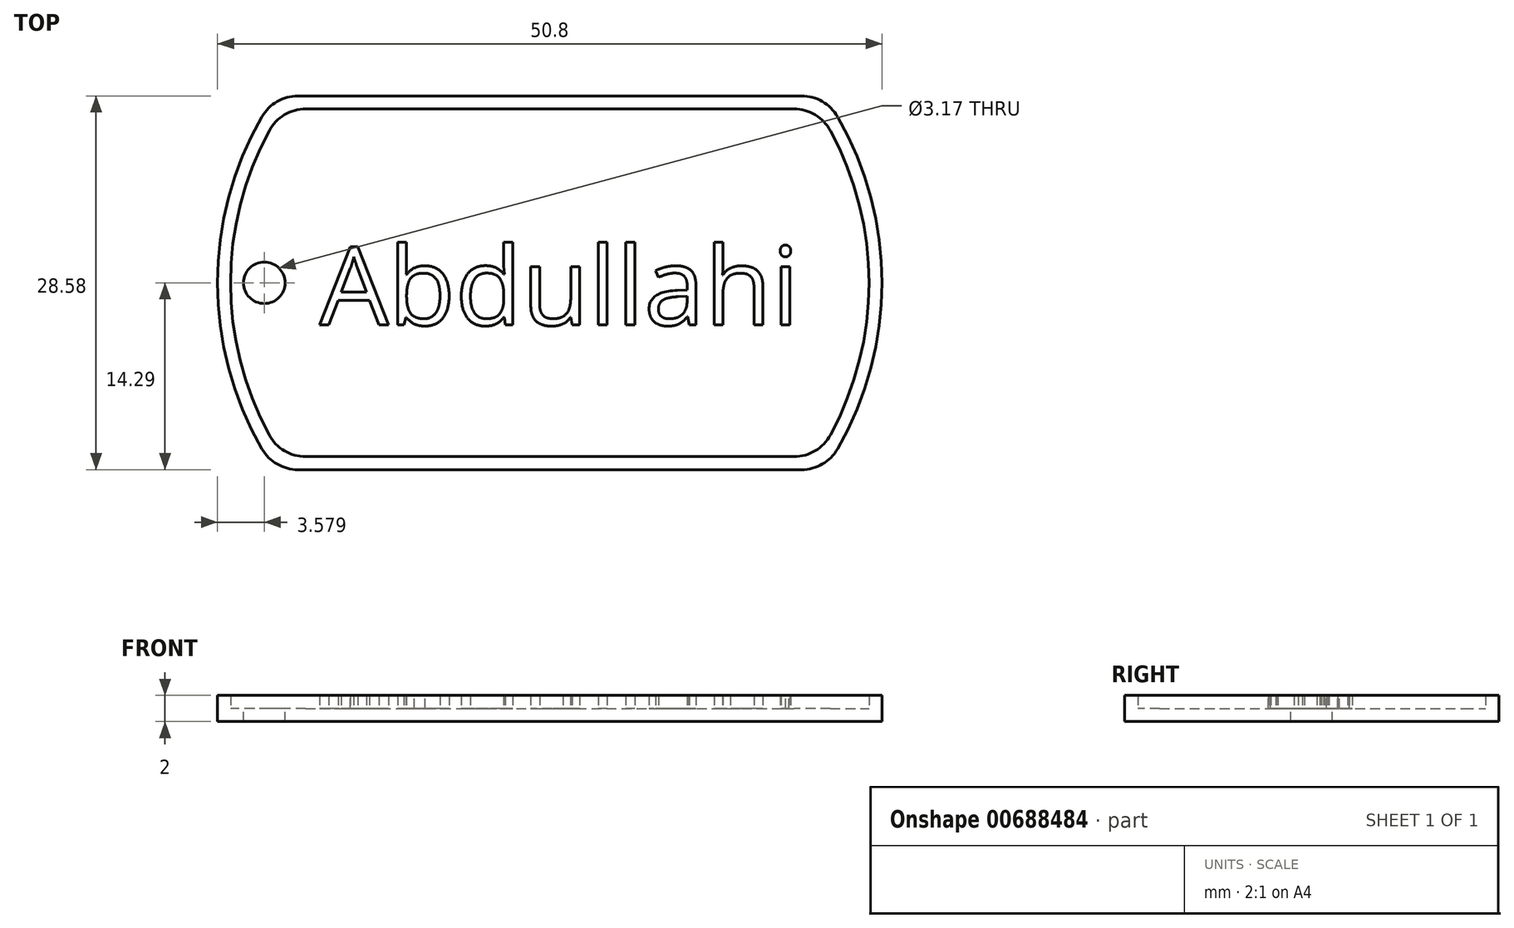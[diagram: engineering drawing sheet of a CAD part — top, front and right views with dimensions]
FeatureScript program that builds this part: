
annotation { "Feature Type Name" : "Feature", "Feature Type Description" : "" }
export const myFeature = defineFeature(function(context is Context, id is Id, definition is map)
    precondition{}
    {
        {
            var Q0;
            Q0=qCreatedBy(makeId("Top.planeOp"),FACE);
            var sketch = newSketch(context, id + "F0", { "sketchPlane" : qUnion([Q0])});
            skArc(sketch, "E0", {"start": v(-22, 12.7) * mm, "mid": v(-25.4, 0) * mm, "end": v(-22, -12.7) * mm});
            skLineSegment(sketch, "E1.top", {"start": v(-19.25, -14.29) * mm, "end": v(19.25, -14.29) * mm});
            skArc(sketch, "E2.trimOffspring", {"start": v(22, -12.7) * mm, "mid": v(25.4, 0) * mm, "end": v(22, 12.7) * mm});
            skLineSegment(sketch, "E3", {"start": v(-19.25, 14.29) * mm, "end": v(19.25, 14.29) * mm});
            skPoint(sketch, "E4.visualSharp", {"position": v(-21, 14.29) * mm});
            skArc(sketch, "E4.filletArc", {"start": v(-19.25, 14.29) * mm, "mid": v(-20.83, 13.86) * mm, "end": v(-22, 12.7) * mm});
            skPoint(sketch, "E5.visualSharp", {"position": v(21, 14.29) * mm});
            skArc(sketch, "E5.filletArc", {"start": v(22, 12.7) * mm, "mid": v(20.83, 13.86) * mm, "end": v(19.25, 14.29) * mm});
            skPoint(sketch, "E6.visualSharp", {"position": v(21, -14.29) * mm});
            skArc(sketch, "E6.filletArc", {"start": v(19.25, -14.29) * mm, "mid": v(20.83, -13.86) * mm, "end": v(22, -12.7) * mm});
            skPoint(sketch, "E7.visualSharp", {"position": v(-21, -14.29) * mm});
            skArc(sketch, "E7.filletArc", {"start": v(-22, -12.7) * mm, "mid": v(-20.83, -13.86) * mm, "end": v(-19.25, -14.29) * mm});
            skSolve(sketch);
        }
        {
            var Q0;
            Q0=makeQuery(id+"F0.imprint","IMPRINT",FACE,{"disambiguationData":[TD([[makeQuery(id+"F0.imprint","IMPRINT",EDGE,{"derivedFrom":sQuery(id+"F0.wireOp",EDGE,"E0")}),1.0]])]});
            extrude(context, id + "F1", {"entities" : qUnion([Q0]), "depth" : 1 * mm, "offsetDistance" : 25.4 * mm});
        }
        {
            var Q0;
            Q0=makeQuery(id+"F1.opExtrude","CAP_FACE",FACE,{"disambiguationData":[OSD([sQuery(id+"F0.wireOp",EDGE,"E0"),sQuery(id+"F0.wireOp",EDGE,"E1.top"),sQuery(id+"F0.wireOp",EDGE,"E2.trimOffspring"),sQuery(id+"F0.wireOp",EDGE,"E3"),sQuery(id+"F0.wireOp",EDGE,"E4.filletArc"),sQuery(id+"F0.wireOp",EDGE,"E5.filletArc"),sQuery(id+"F0.wireOp",EDGE,"E6.filletArc"),sQuery(id+"F0.wireOp",EDGE,"E7.filletArc")])],"isStart":false});
            var sketch = newSketch(context, id + "F2", { "sketchPlane" : qUnion([Q0])});
            skLineSegment(sketch, "E8.0", {"start": v(-18.66, 13.29) * mm, "end": v(18.66, 13.29) * mm});
            skArc(sketch, "E8.1", {"start": v(-21.45, 11.63) * mm, "mid": v(-24.4, 0) * mm, "end": v(-21.45, -11.63) * mm});
            skLineSegment(sketch, "E8.2", {"start": v(-18.66, -13.29) * mm, "end": v(18.66, -13.29) * mm});
            skArc(sketch, "E8.3", {"start": v(21.45, -11.63) * mm, "mid": v(24.4, 0) * mm, "end": v(21.45, 11.63) * mm});
            skPoint(sketch, "E9.visualSharp", {"position": v(-20.46, 13.29) * mm});
            skArc(sketch, "E9.filletArc", {"start": v(-18.66, 13.29) * mm, "mid": v(-20.29, 12.84) * mm, "end": v(-21.45, 11.63) * mm});
            skPoint(sketch, "E10.visualSharp", {"position": v(20.46, 13.29) * mm});
            skArc(sketch, "E10.filletArc", {"start": v(21.45, 11.63) * mm, "mid": v(20.29, 12.84) * mm, "end": v(18.66, 13.29) * mm});
            skPoint(sketch, "E11.visualSharp", {"position": v(20.46, -13.29) * mm});
            skArc(sketch, "E11.filletArc", {"start": v(18.66, -13.29) * mm, "mid": v(20.29, -12.84) * mm, "end": v(21.45, -11.63) * mm});
            skPoint(sketch, "E12.visualSharp", {"position": v(-20.46, -13.29) * mm});
            skArc(sketch, "E12.filletArc", {"start": v(-21.45, -11.63) * mm, "mid": v(-20.29, -12.84) * mm, "end": v(-18.66, -13.29) * mm});
            skLineSegment(sketch, "E13.0", {"start": v(-19.25, 14.29) * mm, "end": v(19.25, 14.29) * mm});
            skArc(sketch, "E13.1", {"start": v(-22, 12.7) * mm, "mid": v(-25.4, 0) * mm, "end": v(-22, -12.7) * mm});
            skLineSegment(sketch, "E13.2", {"start": v(-19.25, -14.29) * mm, "end": v(19.25, -14.29) * mm});
            skArc(sketch, "E13.3", {"start": v(22, -12.7) * mm, "mid": v(25.4, 0) * mm, "end": v(22, 12.7) * mm});
            skPoint(sketch, "E14.visualSharp", {"position": v(-21, -14.29) * mm});
            skArc(sketch, "E14.filletArc", {"start": v(-22, -12.7) * mm, "mid": v(-20.83, -13.86) * mm, "end": v(-19.25, -14.29) * mm});
            skPoint(sketch, "E15.visualSharp", {"position": v(21, -14.29) * mm});
            skArc(sketch, "E15.filletArc", {"start": v(19.25, -14.29) * mm, "mid": v(20.83, -13.86) * mm, "end": v(22, -12.7) * mm});
            skPoint(sketch, "E16.visualSharp", {"position": v(21, 14.29) * mm});
            skArc(sketch, "E16.filletArc", {"start": v(22, 12.7) * mm, "mid": v(20.83, 13.86) * mm, "end": v(19.25, 14.29) * mm});
            skPoint(sketch, "E17.visualSharp", {"position": v(-21, 14.29) * mm});
            skArc(sketch, "E17.filletArc", {"start": v(-19.25, 14.29) * mm, "mid": v(-20.83, 13.86) * mm, "end": v(-22, 12.7) * mm});
            skSolve(sketch);
        }
        {
            var Q0;
            Q0=makeQuery(id+"F2.imprint","IMPRINT",FACE,{"disambiguationData":[TD([[makeQuery(id+"F2.imprint","IMPRINT",EDGE,{"derivedFrom":sQuery(id+"F2.wireOp",EDGE,"E8.0")}),1.0]])]});
            extrude(context, id + "F3", {"entities" : qUnion([Q0]), "operationType" : NewBodyOperationType.ADD, "depth" : 1 * mm, "offsetDistance" : 25.4 * mm});
        }
        {
            var Q0;
            Q0=makeQuery(id+"F1.opExtrude","CAP_FACE",FACE,{"disambiguationData":[OSD([sQuery(id+"F0.wireOp",EDGE,"E0"),sQuery(id+"F0.wireOp",EDGE,"E1.top"),sQuery(id+"F0.wireOp",EDGE,"E2.trimOffspring"),sQuery(id+"F0.wireOp",EDGE,"E3"),sQuery(id+"F0.wireOp",EDGE,"E4.filletArc"),sQuery(id+"F0.wireOp",EDGE,"E5.filletArc"),sQuery(id+"F0.wireOp",EDGE,"E6.filletArc"),sQuery(id+"F0.wireOp",EDGE,"E7.filletArc")])],"isStart":false});
            var sketch = newSketch(context, id + "F4", { "sketchPlane" : qUnion([Q0])});
            skCircle(sketch, "E18", {"center": v(-21.82, 0) * mm, "radius": 1.59 * mm});
            skSolve(sketch);
        }
        {
            var Q0;
            Q0=makeQuery(id+"F4.imprint","IMPRINT",FACE,{"disambiguationData":[TD([[makeQuery(id+"F4.imprint","IMPRINT",EDGE,{"derivedFrom":sQuery(id+"F4.wireOp",EDGE,"E18")}),1.0]])]});
            extrude(context, id + "F5", {"entities" : qUnion([Q0]), "operationType" : NewBodyOperationType.REMOVE, "oppositeDirection" : true, "depth" : 1 * mm, "offsetDistance" : 25.4 * mm});
        }
        {
            var Q0;
            Q0=makeQuery(id+"F2.imprint","IMPRINT",FACE,{"disambiguationData":[TD([[makeQuery(id+"F2.imprint","IMPRINT",EDGE,{"derivedFrom":sQuery(id+"F2.wireOp",EDGE,"E8.0")}),-1.0]])]});
            var sketch = newSketch(context, id + "F6", { "sketchPlane" : qUnion([Q0])});
            skSolve(sketch);
        }
        {
            var Q0;
            Q0=makeQuery(id+"F6.imprint","IMPRINT",FACE,{"disambiguationData":[TD([[makeQuery(id+"F6.imprint","IMPRINT",EDGE,{"derivedFrom":makeQuery(id+"F2.imprint","IMPRINT",EDGE,{"derivedFrom":sQuery(id+"F2.wireOp",EDGE,"E8.0")})}),-1.0]])]});
            var sketch = newSketch(context, id + "F7", { "sketchPlane" : qUnion([Q0])});
            skText(sketch, "E19", { "text": "Abdullahi", "fontName": "OpenSans-Regular.ttf"});
            const initialGuessF7  = {"E19": [-0.01761, -0.00323, 1, 0, 0.006]};
            skSetInitialGuess(sketch, initialGuessF7);
            skSolve(sketch);
        }
        {
            var Q0;
            Q0 = qSketchRegion(id + "F7", true);
            extrude(context, id + "F8", {"entities" : qUnion([Q0]), "operationType" : NewBodyOperationType.ADD, "depth" : 1 * mm, "offsetDistance" : 25.4 * mm});
        }
    });
